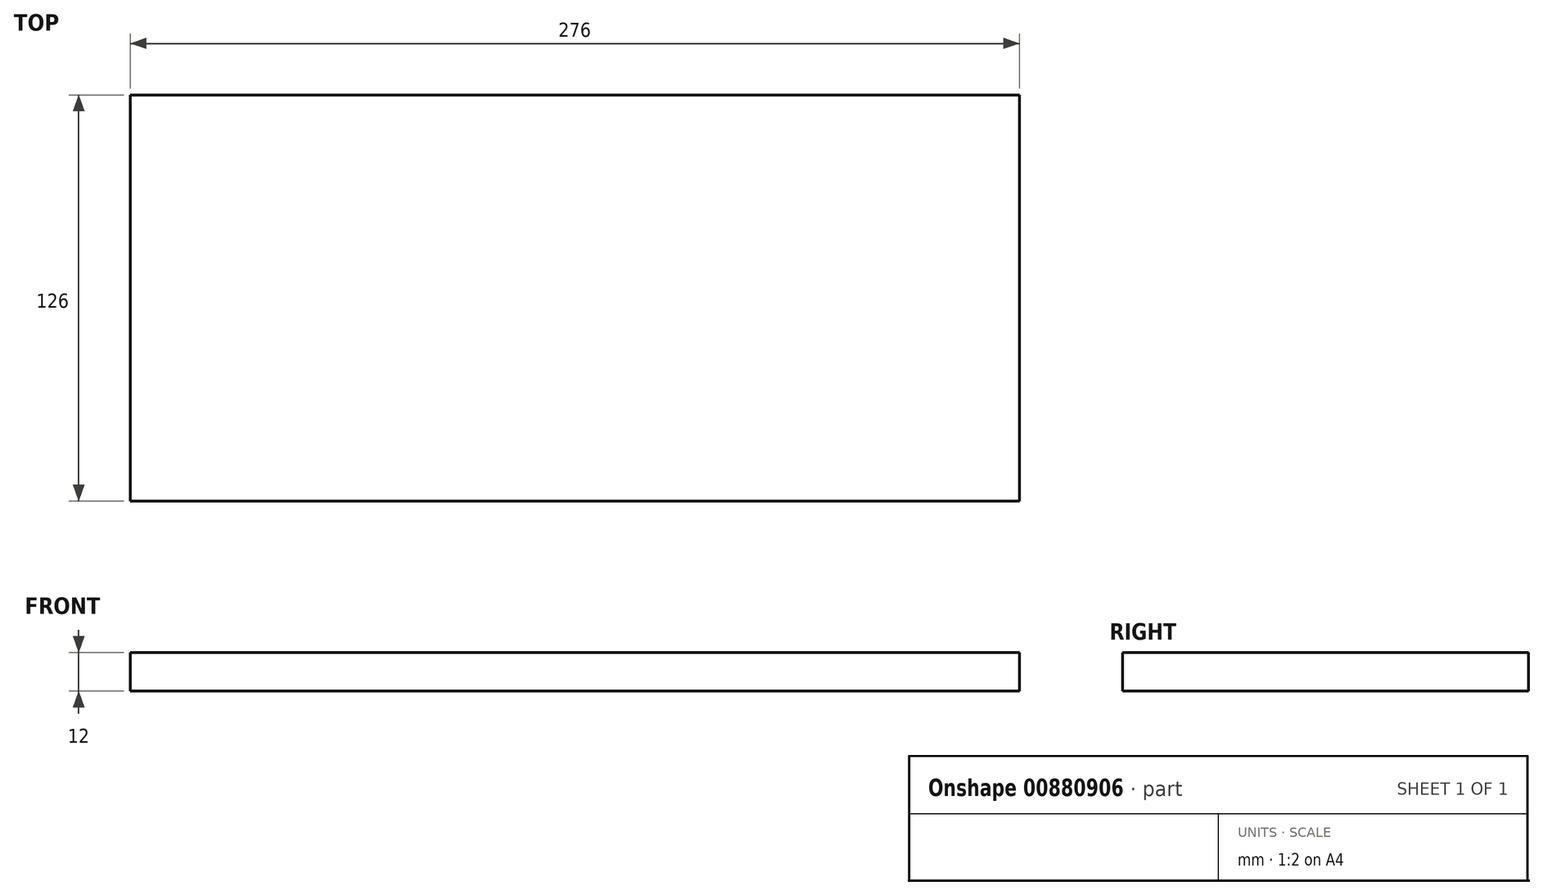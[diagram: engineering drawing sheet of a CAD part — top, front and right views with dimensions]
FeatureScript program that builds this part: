
annotation { "Feature Type Name" : "Feature", "Feature Type Description" : "" }
export const myFeature = defineFeature(function(context is Context, id is Id, definition is map)
    precondition{}
    {
        {
            var Q0;
            Q0=qCreatedBy(makeId("Top.planeOp"),FACE);
            var sketch = newSketch(context, id + "F0", { "sketchPlane" : qUnion([Q0])});
            skLineSegment(sketch, "E0.bottom", {"start": v(138, 63) * mm, "end": v(-138, 63) * mm});
            skLineSegment(sketch, "E0.top", {"start": v(138, -63) * mm, "end": v(-138, -63) * mm});
            skLineSegment(sketch, "E0.left", {"start": v(138, 63) * mm, "end": v(138, -63) * mm});
            skLineSegment(sketch, "E0.right", {"start": v(-138, 63) * mm, "end": v(-138, -63) * mm});
            skPoint(sketch, "E0.middle", {"position": v(0, 0) * mm});
            skSolve(sketch);
        }
        {
            var Q0;
            Q0=makeQuery(id+"F0.imprint","IMPRINT",FACE,{"disambiguationData":[TD([[makeQuery(id+"F0.imprint","IMPRINT",EDGE,{"derivedFrom":sQuery(id+"F0.wireOp",EDGE,"E0.bottom")}),1.0]])]});
            extrude(context, id + "F1", {"entities" : qUnion([Q0]), "depth" : 12 * mm, "offsetDistance" : 25 * mm});
        }
    });
